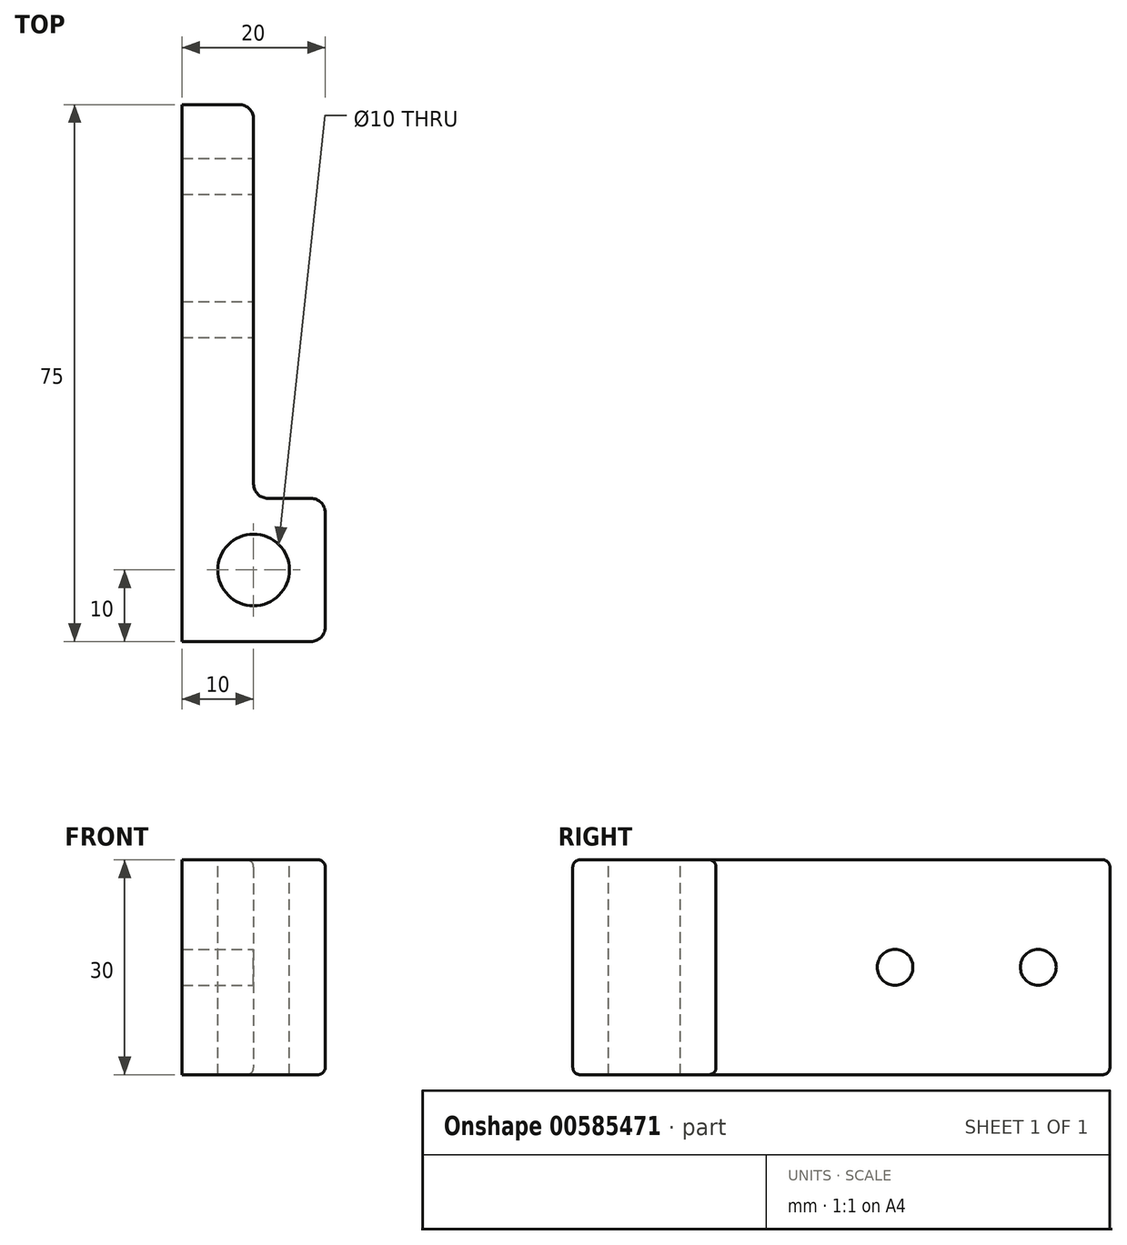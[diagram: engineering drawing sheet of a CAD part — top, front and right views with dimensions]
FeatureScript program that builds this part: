
annotation { "Feature Type Name" : "Feature", "Feature Type Description" : "" }
export const myFeature = defineFeature(function(context is Context, id is Id, definition is map)
    precondition{}
    {
        {
            var Q0;
            Q0=qCreatedBy(makeId("Top.planeOp"),FACE);
            var sketch = newSketch(context, id + "F0", { "sketchPlane" : qUnion([Q0])});
            skLineSegment(sketch, "E0", {"start": v(0, 0) * mm, "end": v(0, -75) * mm});
            skLineSegment(sketch, "E1", {"start": v(0, -75) * mm, "end": v(20, -75) * mm});
            skLineSegment(sketch, "E2", {"start": v(20, -75) * mm, "end": v(20, -55) * mm});
            skLineSegment(sketch, "E3", {"start": v(20, -55) * mm, "end": v(10, -55) * mm});
            skLineSegment(sketch, "E4", {"start": v(10, -55) * mm, "end": v(10, 0) * mm});
            skLineSegment(sketch, "E5", {"start": v(10, 0) * mm, "end": v(0, 0) * mm});
            skSolve(sketch);
        }
        {
            var Q0;
            Q0 = qSketchRegion(id + "F0", true);
            extrude(context, id + "F1", {"entities" : qUnion([Q0]), "depth" : 30 * mm, "offsetDistance" : 25 * mm});
        }
        {
            var Q0;
            Q0=makeQuery(id+"F1.opExtrude","CAP_FACE",FACE,{"disambiguationData":[OSD([sQuery(id+"F0.wireOp",EDGE,"E0"),sQuery(id+"F0.wireOp",EDGE,"E1"),sQuery(id+"F0.wireOp",EDGE,"E2"),sQuery(id+"F0.wireOp",EDGE,"E3"),sQuery(id+"F0.wireOp",EDGE,"E4"),sQuery(id+"F0.wireOp",EDGE,"E5")])],"isStart":false});
            var sketch = newSketch(context, id + "F2", { "sketchPlane" : qUnion([Q0])});
            skLineSegment(sketch, "E6", {"start": v(20, -65) * mm, "end": v(0, -65) * mm});
            skPoint(sketch, "E7", {"position": v(10, -65) * mm});
            skSolve(sketch);
        }
        {
            var Q0;
            Q0=sQuery(id+"F2.wireOp",VERTEX,"E7");
            var Q1;
            Q1=makeQuery(id+"F1.opExtrude","SWEPT_BODY",BODY,{"disambiguationData":[OSD([sQuery(id+"F0.wireOp",EDGE,"E0"),sQuery(id+"F0.wireOp",EDGE,"E1"),sQuery(id+"F0.wireOp",EDGE,"E2"),sQuery(id+"F0.wireOp",EDGE,"E3"),sQuery(id+"F0.wireOp",EDGE,"E4"),sQuery(id+"F0.wireOp",EDGE,"E5")])]});
            hole(context, id + "F3", {"style" : HoleStyle.SIMPLE, "endStyle" : HoleEndStyle.THROUGH, "holeDiameter" : 10 * mm, "majorDiameter" : 5 * mm, "isTappedThrough" : true, "tappedDepth" : 12 * mm, "tapClearance" : 3, "locations" : qUnion([Q0]), "scope" : qUnion([Q1])});
        }
        {
            var Q0;
            Q0=makeQuery(id+"F1.opExtrude","SWEPT_FACE",FACE,{"disambiguationData":[OSD([sQuery(id+"F0.wireOp",EDGE,"E4")])]});
            var sketch = newSketch(context, id + "F4", { "sketchPlane" : qUnion([Q0])});
            skLineSegment(sketch, "E8", {"start": v(0, 15) * mm, "end": v(-26.63, 15) * mm});
            skPoint(sketch, "E9", {"position": v(-10, 15) * mm});
            skSolve(sketch);
        }
        {
            var Q0;
            Q0=sQuery(id+"F4.wireOp",VERTEX,"E9");
            var Q1;
            Q1=makeQuery(id+"F1.opExtrude","SWEPT_BODY",BODY,{"disambiguationData":[OSD([sQuery(id+"F0.wireOp",EDGE,"E0"),sQuery(id+"F0.wireOp",EDGE,"E1"),sQuery(id+"F0.wireOp",EDGE,"E2"),sQuery(id+"F0.wireOp",EDGE,"E3"),sQuery(id+"F0.wireOp",EDGE,"E4"),sQuery(id+"F0.wireOp",EDGE,"E5")])]});
            hole(context, id + "F5", {"style" : HoleStyle.SIMPLE, "endStyle" : HoleEndStyle.THROUGH, "holeDiameter" : 5 * mm, "majorDiameter" : 5 * mm, "isTappedThrough" : true, "tappedDepth" : 12 * mm, "tapClearance" : 3, "locations" : qUnion([Q0]), "scope" : qUnion([Q1])});
        }
        {
            var Q0;
            Q0=makeQuery(id+"F1.opExtrude","SWEPT_FACE",FACE,{"disambiguationData":[OSD([sQuery(id+"F0.wireOp",EDGE,"E4")])]});
            var sketch = newSketch(context, id + "F6", { "sketchPlane" : qUnion([Q0])});
            skLineSegment(sketch, "E10", {"start": v(0, 15) * mm, "end": v(-28.1, 15) * mm});
            skPoint(sketch, "E11", {"position": v(-30, 15) * mm});
            skSolve(sketch);
        }
        {
            var Q0;
            Q0=sQuery(id+"F6.wireOp",VERTEX,"E11");
            var Q1;
            Q1=makeQuery(id+"F1.opExtrude","SWEPT_BODY",BODY,{"disambiguationData":[OSD([sQuery(id+"F0.wireOp",EDGE,"E0"),sQuery(id+"F0.wireOp",EDGE,"E1"),sQuery(id+"F0.wireOp",EDGE,"E2"),sQuery(id+"F0.wireOp",EDGE,"E3"),sQuery(id+"F0.wireOp",EDGE,"E4"),sQuery(id+"F0.wireOp",EDGE,"E5")])]});
            hole(context, id + "F7", {"style" : HoleStyle.SIMPLE, "endStyle" : HoleEndStyle.THROUGH, "holeDiameter" : 5 * mm, "majorDiameter" : 5 * mm, "isTappedThrough" : true, "tappedDepth" : 12 * mm, "tapClearance" : 3, "locations" : qUnion([Q0]), "scope" : qUnion([Q1])});
        }
        {
            var Q0;
            Q0=makeQuery(id+"F1.opExtrude","SWEPT_EDGE",EDGE,{"disambiguationData":[OSD([sQuery(id+"F0.wireOp",EDGE,"E4"),sQuery(id+"F0.wireOp",EDGE,"E5")])]});
            var Q1;
            Q1=makeQuery(id+"F1.opExtrude","SWEPT_EDGE",EDGE,{"disambiguationData":[OSD([sQuery(id+"F0.wireOp",EDGE,"E2"),sQuery(id+"F0.wireOp",EDGE,"E3")])]});
            var Q2;
            Q2=makeQuery(id+"F1.opExtrude","SWEPT_EDGE",EDGE,{"disambiguationData":[OSD([sQuery(id+"F0.wireOp",EDGE,"E3"),sQuery(id+"F0.wireOp",EDGE,"E4")])]});
            var Q3;
            Q3=makeQuery(id+"F1.opExtrude","SWEPT_EDGE",EDGE,{"disambiguationData":[OSD([sQuery(id+"F0.wireOp",EDGE,"E1"),sQuery(id+"F0.wireOp",EDGE,"E2")])]});
            fillet(context, id + "F8", {"entities" : qUnion([Q0, Q1, Q2, Q3]), "radius" : 2 * mm, "tangentPropagation" : true, "allowEdgeOverflow" : false});
        }
        {
            var Q0;
            Q0=makeQuery(id+"F1.opExtrude","CAP_EDGE",EDGE,{"disambiguationData":[OSD([sQuery(id+"F0.wireOp",EDGE,"E5")])],"isStart":false});
            var Q1;
            Q1=makeQuery(id+"F1.opExtrude","CAP_EDGE",EDGE,{"disambiguationData":[OSD([sQuery(id+"F0.wireOp",EDGE,"E4")])],"isStart":true});
            fillet(context, id + "F9", {"entities" : qUnion([Q0, Q1]), "radius" : 1 * mm, "tangentPropagation" : true, "allowEdgeOverflow" : false});
        }
    });
